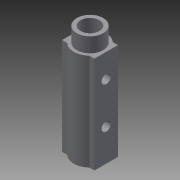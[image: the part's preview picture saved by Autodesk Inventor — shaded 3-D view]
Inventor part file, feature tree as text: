
AUTODESK INVENTOR PART (.ipt)
format: ipt  version: 2015 (Build 190159000, 159)  size: 116,736 bytes
history: native  units: in
note: dims shown in document units (in); Inventor stores cm internally (conversion verified against a paired STEP export)
features: extrude x3, sketch x1
ambient origin geometry x8: Origin, YZ Plane, XZ Plane, XY Plane, X Axis, Y Axis, Z Axis, Center Point
bodies: Body1 (feature_tree)
feature tree (4):
  extrude  "Extrusion3"  Depth=0.4331in
  extrude  "Extrusion4"  Depth=0.1575in
  extrude  "Extrusion5"  Depth=0.315in
  sketch  "Sketch3"  dims[d0=0.252in d1=0.4331in d13=0.1575in d14=0.315in d15=0.315in d16=0.5906in d17=0.0in d18=0.3543in d19=0.7874in d20=0.0in d21=0.2756in d22=0.2756in d23=0.122in d24=0.122in d25=0.7874in d26=0.0in d27=0.7087in d28=0.0in]
